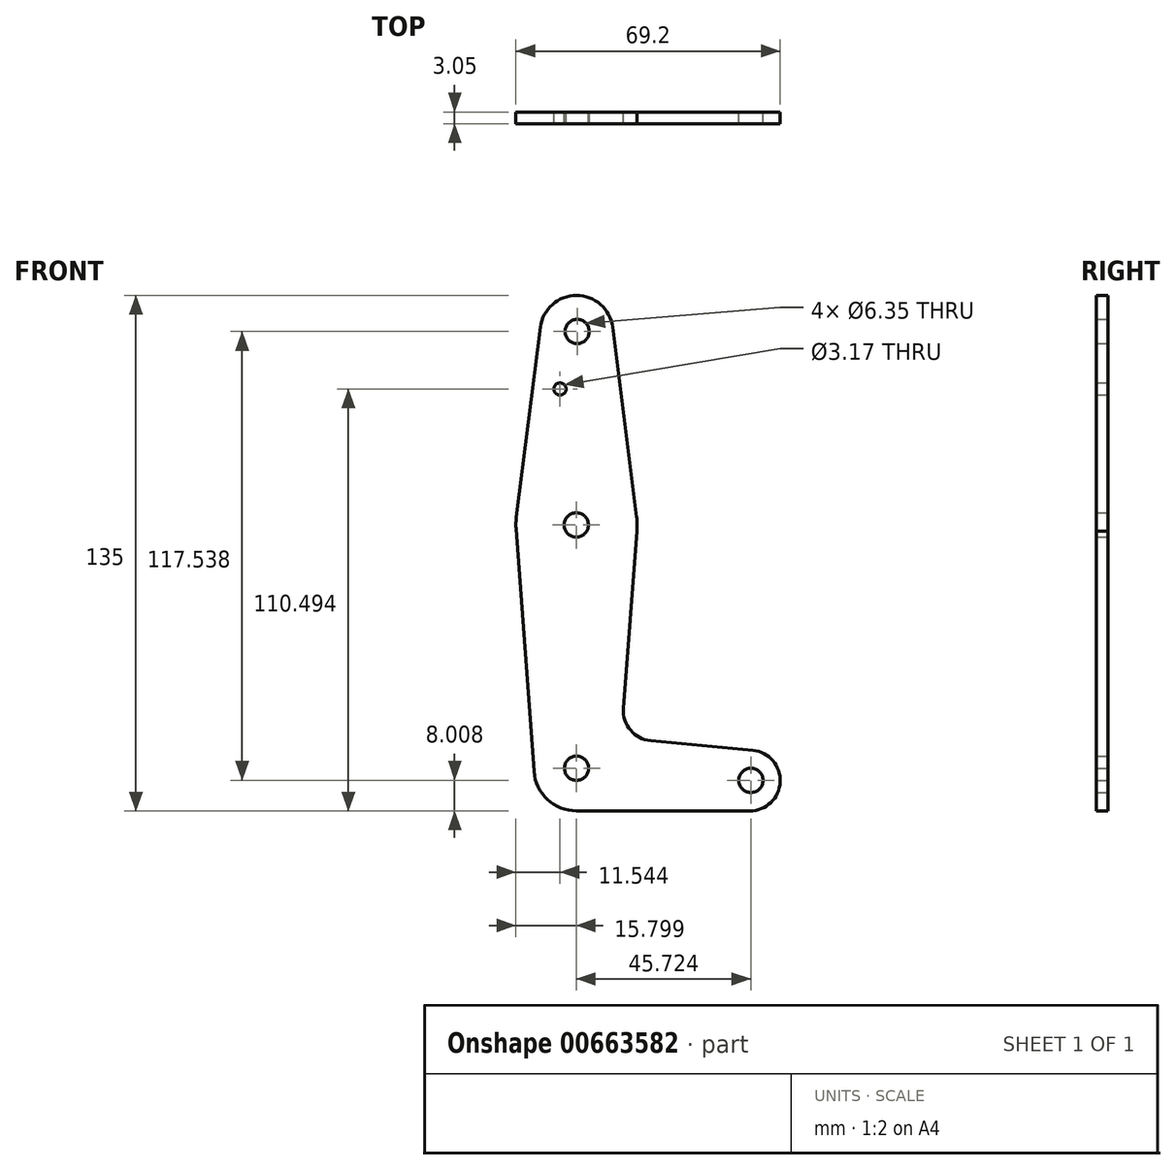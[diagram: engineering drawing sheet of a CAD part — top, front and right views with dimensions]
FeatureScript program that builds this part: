
annotation { "Feature Type Name" : "Feature", "Feature Type Description" : "" }
export const myFeature = defineFeature(function(context is Context, id is Id, definition is map)
    precondition{}
    {
        {
            var Q0;
            Q0=qCreatedBy(makeId("Front.planeOp"),FACE);
            var sketch = newSketch(context, id + "F0", { "sketchPlane" : qUnion([Q0])});
            skLineSegment(sketch, "E0", {"start": v(-2.21, 47.54) * mm, "end": v(-2.21, 9.65) * mm});
            skLineSegment(sketch, "E1", {"start": v(-2.21, -56.87) * mm, "end": v(-2.13, -56.87) * mm});
            skCircle(sketch, "E2", {"center": v(-2.21, 57.07) * mm, "radius": 9.53 * mm});
            skCircle(sketch, "E3", {"center": v(-2.21, 6.52) * mm, "radius": 15.88 * mm});
            skCircle(sketch, "E4", {"center": v(-2.21, -57.23) * mm, "radius": 11.18 * mm});
            skCircle(sketch, "E5", {"center": v(43.17, -60.47) * mm, "radius": 7.94 * mm});
            skLineSegment(sketch, "E6", {"start": v(-2.13, -57.1) * mm, "end": v(-2.13, -56.87) * mm});
            skLineSegment(sketch, "E7", {"start": v(-2.21, -68.4) * mm, "end": v(43.17, -68.4) * mm});
            skLineSegment(sketch, "E8", {"start": v(17.23, -50.05) * mm, "end": v(43.92, -52.57) * mm});
            skCircle(sketch, "E9", {"center": v(-2.06, 57.14) * mm, "radius": 3.18 * mm});
            skCircle(sketch, "E10", {"center": v(-2.21, -57.23) * mm, "radius": 3.17 * mm});
            skCircle(sketch, "E11", {"center": v(-2.3, 6.48) * mm, "radius": 3.18 * mm});
            skLineSegment(sketch, "E12", {"start": v(7.23, 58.27) * mm, "end": v(13.53, 8.52) * mm});
            skLineSegment(sketch, "E13.trimOffspring", {"start": v(10.05, -41.53) * mm, "end": v(13.64, 5.73) * mm});
            skArc(sketch, "E14.filletArc", {"start": v(10.05, -41.53) * mm, "mid": v(11.9, -47.26) * mm, "end": v(17.23, -50.05) * mm});
            skCircle(sketch, "E15", {"center": v(43.43, -60.4) * mm, "radius": 3.18 * mm});
            skCircle(sketch, "E16", {"center": v(-6.55, 42.08) * mm, "radius": 1.59 * mm});
            skLineSegment(sketch, "E17", {"start": v(-11.66, 58.27) * mm, "end": v(-17.96, 8.52) * mm});
            skLineSegment(sketch, "E18", {"start": v(-13.36, -58.05) * mm, "end": v(-18.05, 5.35) * mm});
            skLineSegment(sketch, "E19.trimOffspring", {"start": v(-2.13, -46.05) * mm, "end": v(-2.13, 3.3) * mm});
            skLineSegment(sketch, "E20.trimOffspring", {"start": v(-2.21, -56.87) * mm, "end": v(-2.21, -57.23) * mm});
            skLineSegment(sketch, "E21.trimOffspring", {"start": v(8.96, -56.87) * mm, "end": v(42.24, -56.87) * mm});
            skSolve(sketch);
        }
        {
            var Q0;
            Q0 = qSketchRegion(id + "F0", true);
            extrude(context, id + "F1", {"entities" : qUnion([Q0]), "depth" : 3.05 * mm, "offsetDistance" : 25.4 * mm});
        }
    });
